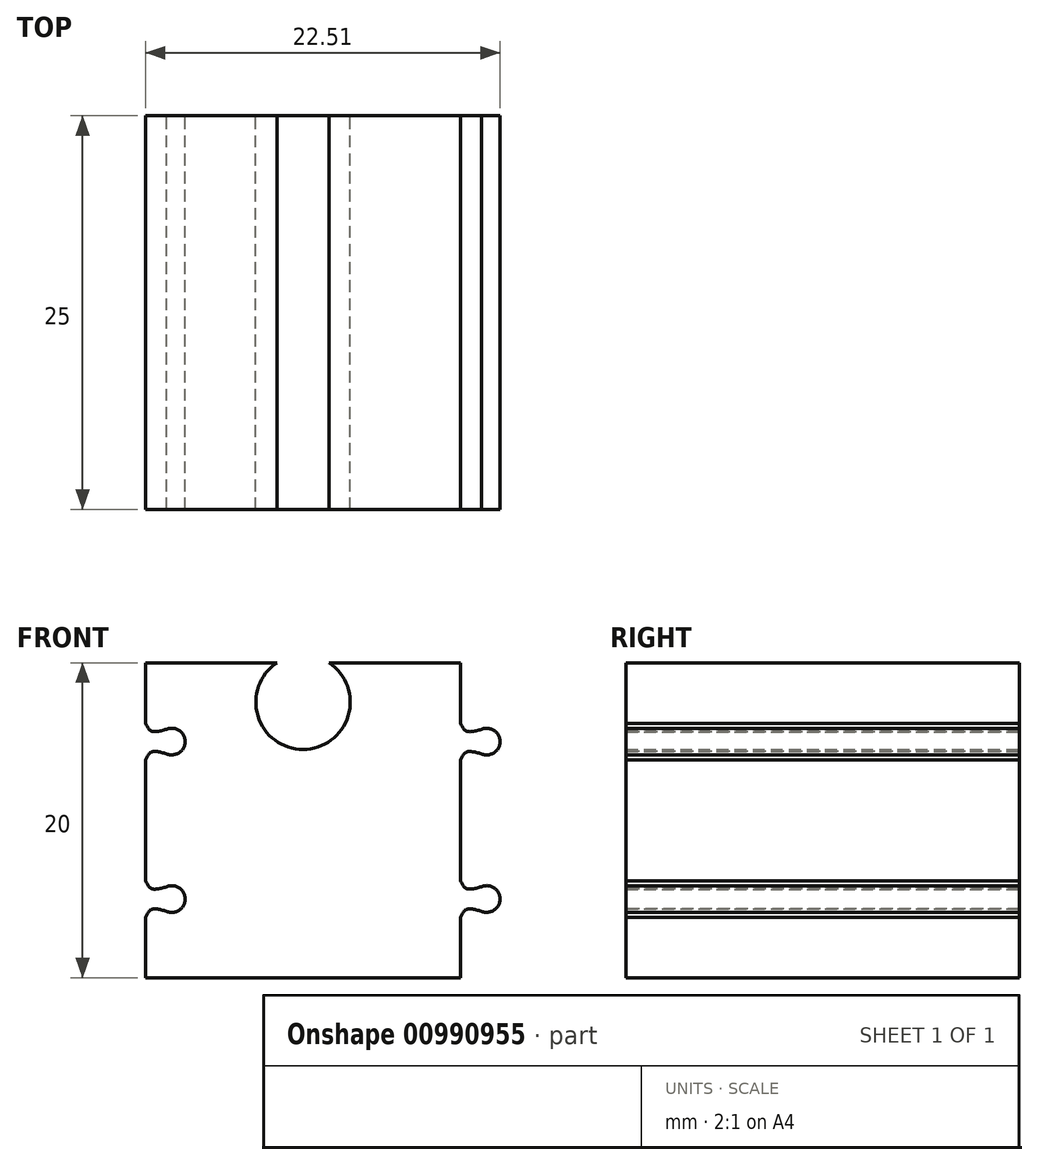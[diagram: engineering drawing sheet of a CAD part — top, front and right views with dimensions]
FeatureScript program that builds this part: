
annotation { "Feature Type Name" : "Feature", "Feature Type Description" : "" }
export const myFeature = defineFeature(function(context is Context, id is Id, definition is map)
    precondition{}
    {
        {
            var Q0;
            Q0=qCreatedBy(makeId("Front.planeOp"),FACE);
            var sketch = newSketch(context, id + "F0", { "sketchPlane" : qUnion([Q0])});
            skLineSegment(sketch, "E0.bottom", {"start": v(10, -10) * mm, "end": v(-10, -10) * mm});
            skLineSegment(sketch, "E0.top", {"start": v(10, 10) * mm, "end": v(-10, 10) * mm});
            skLineSegment(sketch, "E0.left", {"start": v(10, -10) * mm, "end": v(10, 10) * mm});
            skLineSegment(sketch, "E0.right", {"start": v(-10, -10) * mm, "end": v(-10, 10) * mm});
            skPoint(sketch, "E0.middle", {"position": v(0, 0) * mm});
            skPoint(sketch, "E1", {"position": v(0, 5) * mm});
            skPoint(sketch, "E2", {"position": v(0, 7.5) * mm});
            skCircle(sketch, "E3", {"center": v(0, 7.5) * mm, "radius": 3 * mm});
            skLineSegment(sketch, "E4", {"start": v(0, 5) * mm, "end": v(-15.55, 5) * mm, "construction": true});
            skLineSegment(sketch, "E5", {"start": v(0, 0) * mm, "end": v(-12.37, 0) * mm, "construction": true});
            skFitSpline(sketch, "E6", {"points": [v(-10, 6.16) * mm, v(-9.63, 5.67) * mm, v(-8.67, 5.78) * mm], "startDerivative": vector(0.63, -1.4) * mm, "endDerivative": vector(1.98, 0.57) * mm});
            skFitSpline(sketch, "E7.MirrorCS", {"points": [v(-10, 3.84) * mm, v(-9.63, 4.34) * mm, v(-8.67, 4.22) * mm], "startDerivative": vector(0.63, 1.4) * mm, "endDerivative": vector(1.98, -0.57) * mm});
            skArc(sketch, "E8", {"start": v(-8.67, 4.22) * mm, "mid": v(-7.49, 5) * mm, "end": v(-8.67, 5.78) * mm});
            skFitSpline(sketch, "E9.MirrorCS", {"points": [v(-10, -6.16) * mm, v(-9.63, -5.67) * mm, v(-8.67, -5.78) * mm], "startDerivative": vector(0.63, 1.4) * mm, "endDerivative": vector(1.98, -0.57) * mm});
            skFitSpline(sketch, "E10.MirrorCS", {"points": [v(-10, -3.84) * mm, v(-9.63, -4.34) * mm, v(-8.67, -4.22) * mm], "startDerivative": vector(0.63, -1.4) * mm, "endDerivative": vector(1.98, 0.57) * mm});
            skArc(sketch, "E11.MirrorCS", {"start": v(-8.67, -4.22) * mm, "mid": v(-7.49, -5) * mm, "end": v(-8.67, -5.78) * mm});
            skLineSegment(sketch, "E12", {"start": v(0, 13.33) * mm, "end": v(0, -12.08) * mm, "construction": true});
            skFitSpline(sketch, "E13.MirrorCS", {"points": [v(10, 3.84) * mm, v(10.37, 4.33) * mm, v(11.34, 4.22) * mm], "startDerivative": vector(0.63, 1.4) * mm, "endDerivative": vector(1.98, -0.57) * mm});
            skFitSpline(sketch, "E14.MirrorCS", {"points": [v(10, 6.16) * mm, v(10.37, 5.67) * mm, v(11.34, 5.78) * mm], "startDerivative": vector(0.63, -1.4) * mm, "endDerivative": vector(1.98, 0.57) * mm});
            skArc(sketch, "E15.MirrorCS", {"start": v(11.34, 5.78) * mm, "mid": v(12.51, 5) * mm, "end": v(11.34, 4.22) * mm});
            skLineSegment(sketch, "E16.MirrorCS", {"start": v(0, 0) * mm, "end": v(12.37, 0) * mm, "construction": true});
            skLineSegment(sketch, "E17.MirrorCS", {"start": v(0, 5) * mm, "end": v(15.55, 5) * mm, "construction": true});
            skFitSpline(sketch, "E18.MirrorCS", {"points": [v(-10, 3.84) * mm, v(-9.63, 4.33) * mm, v(-8.67, 4.22) * mm], "startDerivative": vector(0.63, 1.4) * mm, "endDerivative": vector(1.98, -0.57) * mm});
            skArc(sketch, "E19.MirrorCS", {"start": v(-8.67, 4.22) * mm, "mid": v(-7.5, 5) * mm, "end": v(-8.67, 5.78) * mm});
            skFitSpline(sketch, "E20.MirrorCS", {"points": [v(10, -6.16) * mm, v(10.37, -5.67) * mm, v(11.34, -5.78) * mm], "startDerivative": vector(0.63, 1.4) * mm, "endDerivative": vector(1.98, -0.57) * mm});
            skFitSpline(sketch, "E21.MirrorCS", {"points": [v(10, -3.84) * mm, v(10.37, -4.33) * mm, v(11.34, -4.22) * mm], "startDerivative": vector(0.63, -1.4) * mm, "endDerivative": vector(1.98, 0.57) * mm});
            skArc(sketch, "E22.MirrorCS", {"start": v(11.34, -5.78) * mm, "mid": v(12.51, -5) * mm, "end": v(11.34, -4.22) * mm});
            skSolve(sketch);
        }
        {
            var Q0;
            {var subQ0=sQuery(id+"F0.wireOp",EDGE,"E13.MirrorCS");Q0=makeQuery(id+"F0.imprint","IMPRINT",FACE,{"disambiguationData":[TD([[makeQuery(id+"F0.imprint","IMPRINT",EDGE,{"derivedFrom":subQ0}),1.0]])]});}
            var Q1;
            {var subQ0=sQuery(id+"F0.wireOp",EDGE,"E20.MirrorCS");Q1=makeQuery(id+"F0.imprint","IMPRINT",FACE,{"disambiguationData":[TD([[makeQuery(id+"F0.imprint","IMPRINT",EDGE,{"derivedFrom":subQ0}),1.0]])]});}
            var Q2;
            {var subQ1=sQuery(id+"F0.wireOp",EDGE,"E7.MirrorCS");Q2=makeQuery(id+"F0.imprint","IMPRINT",FACE,{"disambiguationData":[TD([[makeQuery(id+"F0.imprint","IMPRINT",EDGE,{"derivedFrom":subQ1}),-1.0]])]});}
            var Q3;
            {var subQ9=sQuery(id+"F0.wireOp",EDGE,"E0.bottom");Q3=makeQuery(id+"F0.imprint","IMPRINT",FACE,{"disambiguationData":[TD([[makeQuery(id+"F0.imprint","IMPRINT",EDGE,{"derivedFrom":subQ9}),-1.0]])]});}
            extrude(context, id + "F1", {"entities" : qUnion([Q0, Q1, Q2, Q3]), "depth" : 25 * mm, "offsetDistance" : 25 * mm});
        }
    });
